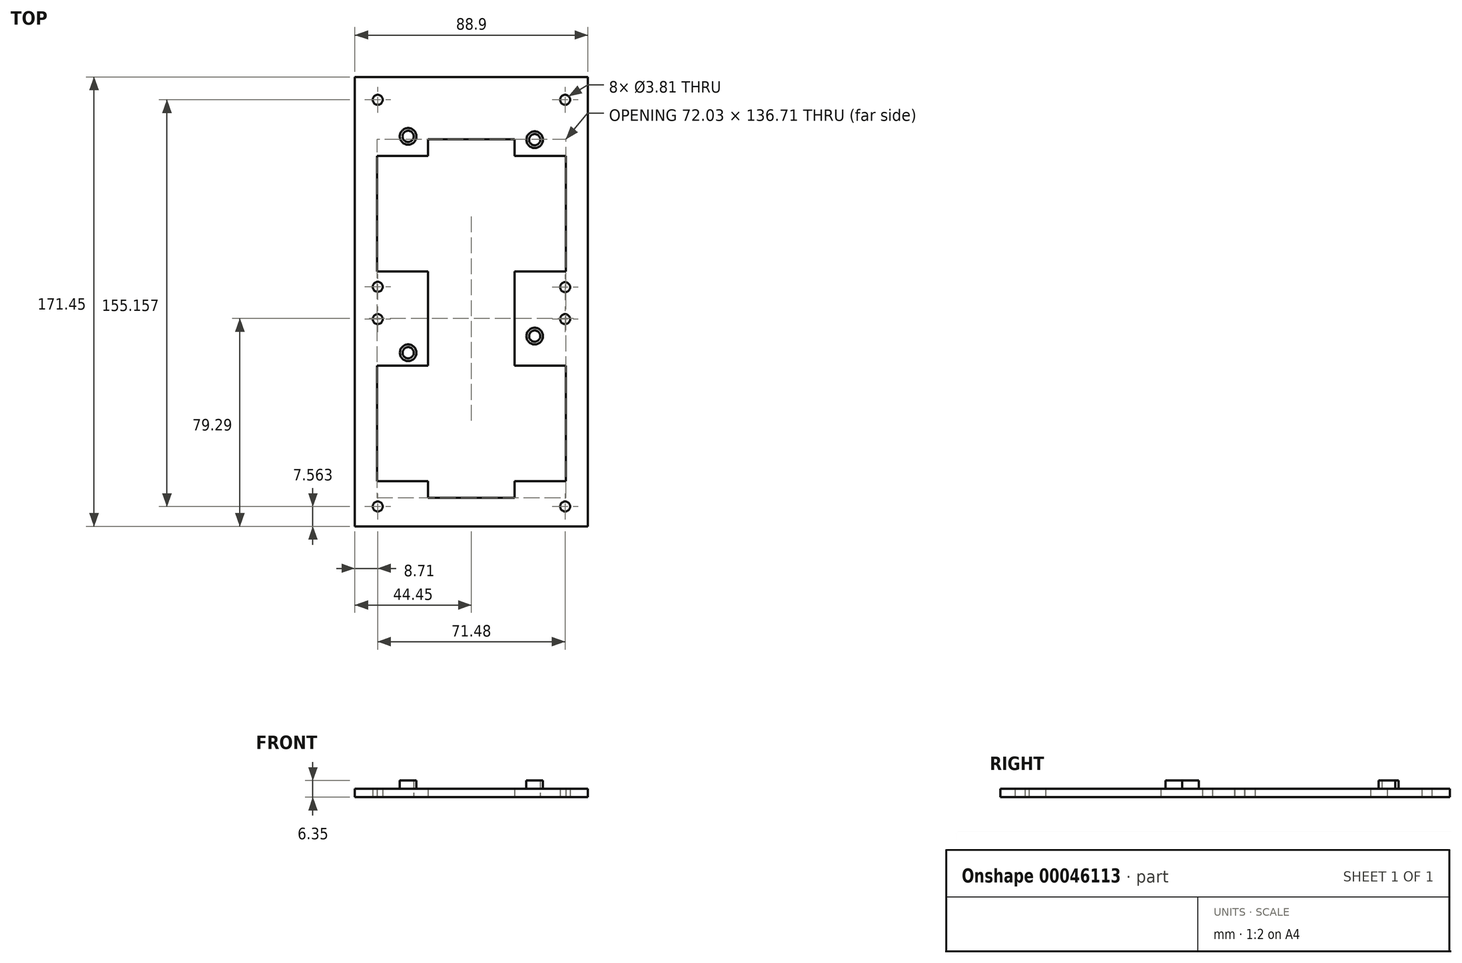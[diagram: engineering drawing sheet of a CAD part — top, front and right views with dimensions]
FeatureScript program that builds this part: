
annotation { "Feature Type Name" : "Feature", "Feature Type Description" : "" }
export const myFeature = defineFeature(function(context is Context, id is Id, definition is map)
    precondition{}
    {
        {
            var Q0;
            Q0=qCreatedBy(makeId("Top.planeOp"),FACE);
            var sketch = newSketch(context, id + "F0", { "sketchPlane" : qUnion([Q0])});
            skLineSegment(sketch, "E0", {"start": v(-44.45, 44.47) * mm, "end": v(44.45, 44.47) * mm});
            skCircle(sketch, "E1", {"center": v(35.74, 35.74) * mm, "radius": 1.9 * mm});
            skCircle(sketch, "E2", {"center": v(-35.74, -35.62) * mm, "radius": 1.9 * mm});
            skCircle(sketch, "E3", {"center": v(-35.74, 35.74) * mm, "radius": 1.9 * mm});
            skCircle(sketch, "E4", {"center": v(35.74, -35.74) * mm, "radius": 1.9 * mm});
            skCircle(sketch, "E5", {"center": v(24.13, 20.5) * mm, "radius": 2.15 * mm});
            skCircle(sketch, "E6", {"center": v(-24.14, 21.77) * mm, "radius": 2.15 * mm});
            skCircle(sketch, "E7", {"center": v(24.13, -54.42) * mm, "radius": 2.15 * mm});
            skCircle(sketch, "E8", {"center": v(-24.13, -60.78) * mm, "radius": 2.15 * mm});
            skLineSegment(sketch, "E9", {"start": v(-16.5, 20.67) * mm, "end": v(16.51, 20.67) * mm});
            skLineSegment(sketch, "E10", {"start": v(-16.5, 20.67) * mm, "end": v(-16.5, 14.32) * mm});
            skLineSegment(sketch, "E11", {"start": v(-16.5, 14.32) * mm, "end": v(-36.01, 14.32) * mm});
            skLineSegment(sketch, "E12", {"start": v(-36.01, 14.32) * mm, "end": v(-36.01, -29.72) * mm});
            skLineSegment(sketch, "E13", {"start": v(-36.01, -29.72) * mm, "end": v(-16.5, -29.72) * mm});
            skLineSegment(sketch, "E14", {"start": v(-16.51, -116.05) * mm, "end": v(16.5, -116.05) * mm});
            skLineSegment(sketch, "E15", {"start": v(36.01, -29.72) * mm, "end": v(16.51, -29.72) * mm});
            skLineSegment(sketch, "E16", {"start": v(36.01, -29.72) * mm, "end": v(36.01, 14.32) * mm});
            skLineSegment(sketch, "E17", {"start": v(16.51, 20.67) * mm, "end": v(16.51, 14.32) * mm});
            skLineSegment(sketch, "E18", {"start": v(16.51, 14.32) * mm, "end": v(36.01, 14.32) * mm});
            skLineSegment(sketch, "E19", {"start": v(-44.45, 44.47) * mm, "end": v(-44.45, -126.98) * mm});
            skCircle(sketch, "E20", {"center": v(35.74, -47.94) * mm, "radius": 1.9 * mm});
            skCircle(sketch, "E21", {"center": v(-35.74, -119.42) * mm, "radius": 1.9 * mm});
            skCircle(sketch, "E22", {"center": v(-35.74, -47.94) * mm, "radius": 1.9 * mm});
            skCircle(sketch, "E23", {"center": v(35.74, -119.42) * mm, "radius": 1.9 * mm});
            skLineSegment(sketch, "E24", {"start": v(44.45, 44.47) * mm, "end": v(44.45, -126.98) * mm});
            skLineSegment(sketch, "E25", {"start": v(-16.51, -65.66) * mm, "end": v(-36.01, -65.66) * mm});
            skLineSegment(sketch, "E26", {"start": v(-36.01, -65.66) * mm, "end": v(-36.01, -109.7) * mm});
            skLineSegment(sketch, "E27", {"start": v(-36.01, -109.7) * mm, "end": v(-16.51, -109.7) * mm});
            skLineSegment(sketch, "E28", {"start": v(36.01, -109.7) * mm, "end": v(16.5, -109.7) * mm});
            skLineSegment(sketch, "E29", {"start": v(36.01, -109.7) * mm, "end": v(36.01, -65.66) * mm});
            skLineSegment(sketch, "E30", {"start": v(16.5, -65.66) * mm, "end": v(36.01, -65.66) * mm});
            skLineSegment(sketch, "E31", {"start": v(-16.51, -109.7) * mm, "end": v(-16.51, -116.05) * mm});
            skLineSegment(sketch, "E32", {"start": v(16.5, -109.7) * mm, "end": v(16.5, -116.05) * mm});
            skLineSegment(sketch, "E33", {"start": v(-16.5, -29.72) * mm, "end": v(-16.51, -65.66) * mm});
            skLineSegment(sketch, "E34", {"start": v(16.51, -29.72) * mm, "end": v(16.5, -65.66) * mm});
            skLineSegment(sketch, "E35", {"start": v(-44.45, -126.98) * mm, "end": v(44.45, -126.98) * mm});
            skCircle(sketch, "E36", {"center": v(-24.14, 21.77) * mm, "radius": 3.17 * mm});
            skCircle(sketch, "E37", {"center": v(24.13, 20.5) * mm, "radius": 3.17 * mm});
            skCircle(sketch, "E38", {"center": v(-24.13, -60.78) * mm, "radius": 3.17 * mm});
            skCircle(sketch, "E39", {"center": v(24.13, -54.42) * mm, "radius": 3.17 * mm});
            skSolve(sketch);
        }
        {
            var Q0;
            Q0 = qSketchRegion(id + "F0", true);
            extrude(context, id + "F1", {"entities" : qUnion([Q0]), "depth" : 3.17 * mm, "offsetDistance" : 25.4 * mm});
        }
        {
            var Q0;
            Q0=makeQuery(id+"F0.imprint","IMPRINT",FACE,{"disambiguationData":[TD([[makeQuery(id+"F0.imprint","IMPRINT",EDGE,{"derivedFrom":sQuery(id+"F0.wireOp",EDGE,"E8")}),-1.0]])]});
            var Q1;
            Q1=makeQuery(id+"F0.imprint","IMPRINT",FACE,{"disambiguationData":[TD([[makeQuery(id+"F0.imprint","IMPRINT",EDGE,{"derivedFrom":sQuery(id+"F0.wireOp",EDGE,"E6")}),-1.0]])]});
            var Q2;
            Q2=makeQuery(id+"F0.imprint","IMPRINT",FACE,{"disambiguationData":[TD([[makeQuery(id+"F0.imprint","IMPRINT",EDGE,{"derivedFrom":sQuery(id+"F0.wireOp",EDGE,"E7")}),-1.0]])]});
            var Q3;
            Q3=makeQuery(id+"F0.imprint","IMPRINT",FACE,{"disambiguationData":[TD([[makeQuery(id+"F0.imprint","IMPRINT",EDGE,{"derivedFrom":sQuery(id+"F0.wireOp",EDGE,"E5")}),-1.0]])]});
            extrude(context, id + "F2", {"entities" : qUnion([Q0, Q1, Q2, Q3]), "operationType" : NewBodyOperationType.ADD, "depth" : 6.35 * mm, "offsetDistance" : 25.4 * mm});
        }
    });
